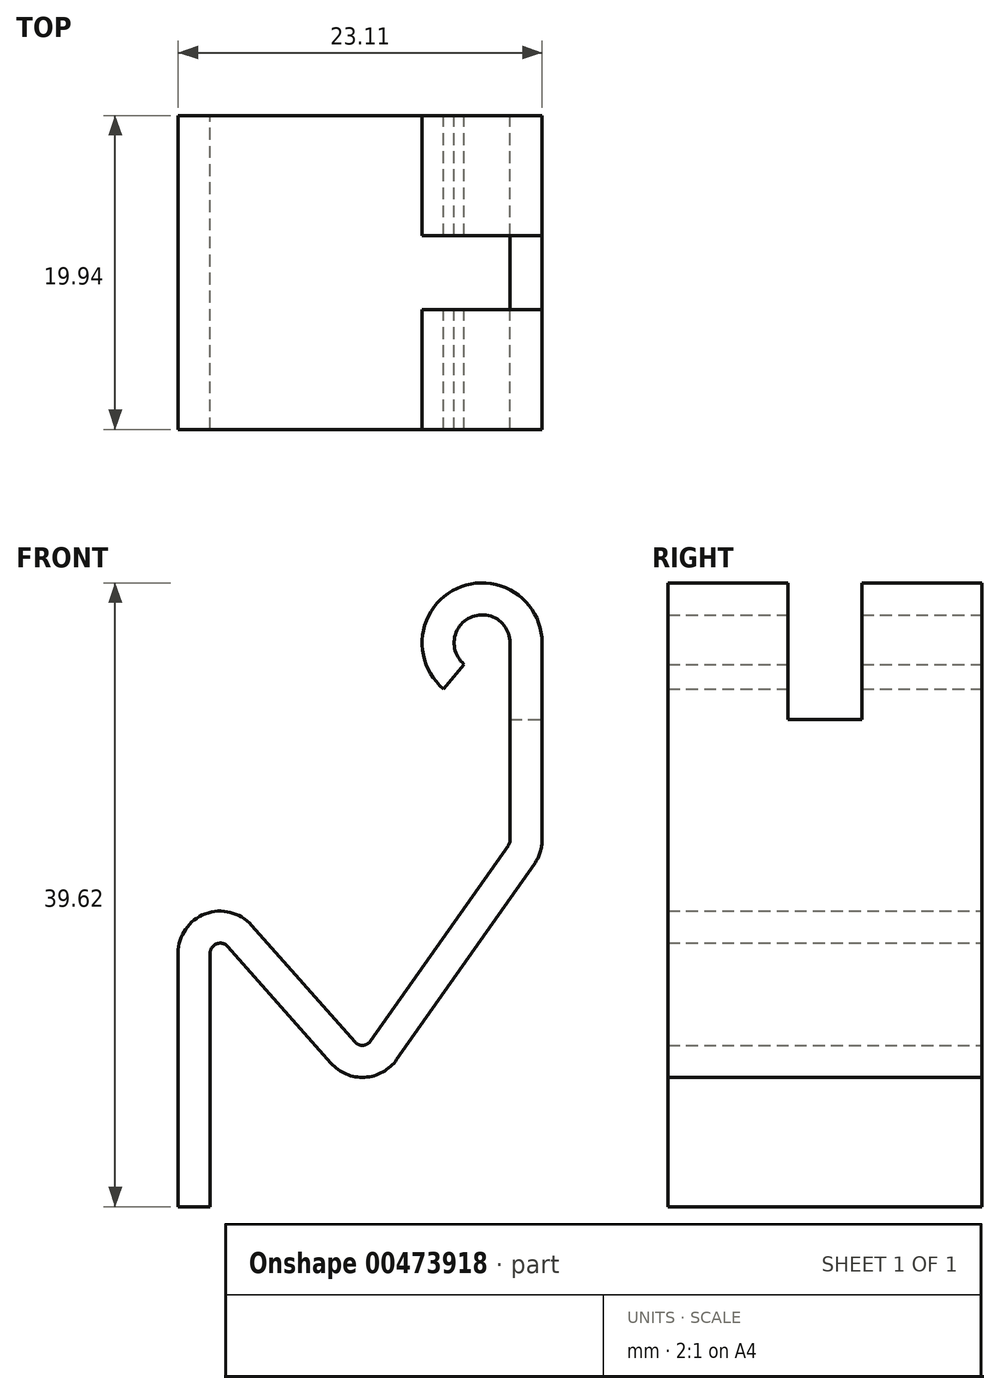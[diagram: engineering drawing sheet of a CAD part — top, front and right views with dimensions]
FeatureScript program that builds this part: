
annotation { "Feature Type Name" : "Feature", "Feature Type Description" : "" }
export const myFeature = defineFeature(function(context is Context, id is Id, definition is map)
    precondition{}
    {
        {
            var Q0;
            Q0=qCreatedBy(makeId("Front.planeOp"),FACE);
            var sketch = newSketch(context, id + "F0", { "sketchPlane" : qUnion([Q0])});
            skLineSegment(sketch, "E0", {"start": v(0, 0) * mm, "end": v(0, 16.1) * mm});
            skLineSegment(sketch, "E1", {"start": v(1.11, 16.53) * mm, "end": v(7.67, 9.11) * mm});
            skLineSegment(sketch, "E2", {"start": v(10.19, 10.52) * mm, "end": v(18.93, 22.95) * mm});
            skLineSegment(sketch, "E3", {"start": v(19.05, 23.31) * mm, "end": v(19.05, 35.81) * mm});
            skArc(sketch, "E4", {"start": v(19.05, 35.81) * mm, "mid": v(16.52, 37.43) * mm, "end": v(16.13, 34.45) * mm});
            skPoint(sketch, "E5.visualSharp", {"position": v(0, 17.78) * mm});
            skArc(sketch, "E5.filletArc", {"start": v(1.11, 16.53) * mm, "mid": v(0.4, 16.7) * mm, "end": v(0, 16.1) * mm});
            skPoint(sketch, "E6.visualSharp", {"position": v(19.05, 23.11) * mm});
            skArc(sketch, "E6.filletArc", {"start": v(18.93, 22.95) * mm, "mid": v(19.02, 23.12) * mm, "end": v(19.05, 23.31) * mm});
            skLineSegment(sketch, "E7.0", {"start": v(2.63, 17.87) * mm, "end": v(9.2, 10.46) * mm});
            skArc(sketch, "E7.1", {"start": v(2.63, 17.87) * mm, "mid": v(-0.31, 18.6) * mm, "end": v(-2.03, 16.1) * mm});
            skLineSegment(sketch, "E7.2", {"start": v(-2.03, 0) * mm, "end": v(-2.03, 16.1) * mm});
            skArc(sketch, "E8.0", {"start": v(21.08, 35.81) * mm, "mid": v(15.66, 39.27) * mm, "end": v(14.82, 32.9) * mm});
            skLineSegment(sketch, "E8.1", {"start": v(21.08, 23.31) * mm, "end": v(21.08, 35.81) * mm});
            skArc(sketch, "E8.2", {"start": v(20.6, 21.78) * mm, "mid": v(20.96, 22.51) * mm, "end": v(21.08, 23.31) * mm});
            skLineSegment(sketch, "E8.3", {"start": v(11.85, 9.35) * mm, "end": v(20.6, 21.78) * mm});
            skArc(sketch, "E9.filletArc", {"start": v(9.2, 10.46) * mm, "mid": v(9.7, 10.25) * mm, "end": v(10.19, 10.52) * mm});
            skArc(sketch, "E10.0", {"start": v(7.67, 9.11) * mm, "mid": v(9.82, 8.22) * mm, "end": v(11.85, 9.35) * mm});
            skLineSegment(sketch, "E11", {"start": v(-2.03, 0) * mm, "end": v(0, 0) * mm});
            skLineSegment(sketch, "E12", {"start": v(16.13, 34.45) * mm, "end": v(14.82, 32.9) * mm});
            skSolve(sketch);
        }
        {
            var Q0;
            Q0=makeQuery(id+"F0.imprint","IMPRINT",FACE,{"disambiguationData":[TD([[makeQuery(id+"F0.imprint","IMPRINT",EDGE,{"derivedFrom":sQuery(id+"F0.wireOp",EDGE,"E0")}),1.0]])]});
            extrude(context, id + "F1", {"entities" : qUnion([Q0]), "depth" : 19.94 * mm});
        }
        {
            var Q0;
            Q0=makeQuery(id+"F1.opExtrude","SWEPT_FACE",FACE,{"disambiguationData":[OSD([sQuery(id+"F0.wireOp",EDGE,"E8.1")])]});
            var sketch = newSketch(context, id + "F2", { "sketchPlane" : qUnion([Q0])});
            skLineSegment(sketch, "E13.0", {"start": v(-19.94, 23.31) * mm, "end": v(-19.94, 35.81) * mm});
            skLineSegment(sketch, "E14.0", {"start": v(0, 23.31) * mm, "end": v(0, 35.81) * mm});
            skLineSegment(sketch, "E15.0", {"start": v(-12.32, 30.93) * mm, "end": v(-12.32, 48.27) * mm});
            skLineSegment(sketch, "E16.0", {"start": v(-7.62, 30.93) * mm, "end": v(-7.62, 48.27) * mm});
            skLineSegment(sketch, "E17.0", {"start": v(-19.94, 23.31) * mm, "end": v(0, 23.31) * mm});
            skLineSegment(sketch, "E18.0", {"start": v(-12.32, 30.93) * mm, "end": v(-7.62, 30.93) * mm});
            skLineSegment(sketch, "E19", {"start": v(-12.32, 48.27) * mm, "end": v(-7.62, 48.27) * mm});
            skSolve(sketch);
        }
        {
            var Q0;
            {var subQ0=sQuery(id+"F2.wireOp",EDGE,"E19");Q0=makeQuery(id+"F2.imprint","IMPRINT",FACE,{"disambiguationData":[TD([[makeQuery(id+"F2.imprint","IMPRINT",EDGE,{"derivedFrom":subQ0}),-1.0]])]});}
            var Q1;
            {var subQ0=sQuery(id+"F2.wireOp",EDGE,"E18.0");Q1=makeQuery(id+"F2.imprint","IMPRINT",FACE,{"disambiguationData":[TD([[makeQuery(id+"F2.imprint","IMPRINT",EDGE,{"derivedFrom":subQ0}),1.0]])]});}
            extrude(context, id + "F3", {"entities" : qUnion([Q0, Q1]), "operationType" : NewBodyOperationType.REMOVE, "oppositeDirection" : true, "depth" : 25.4 * mm});
        }
    });
